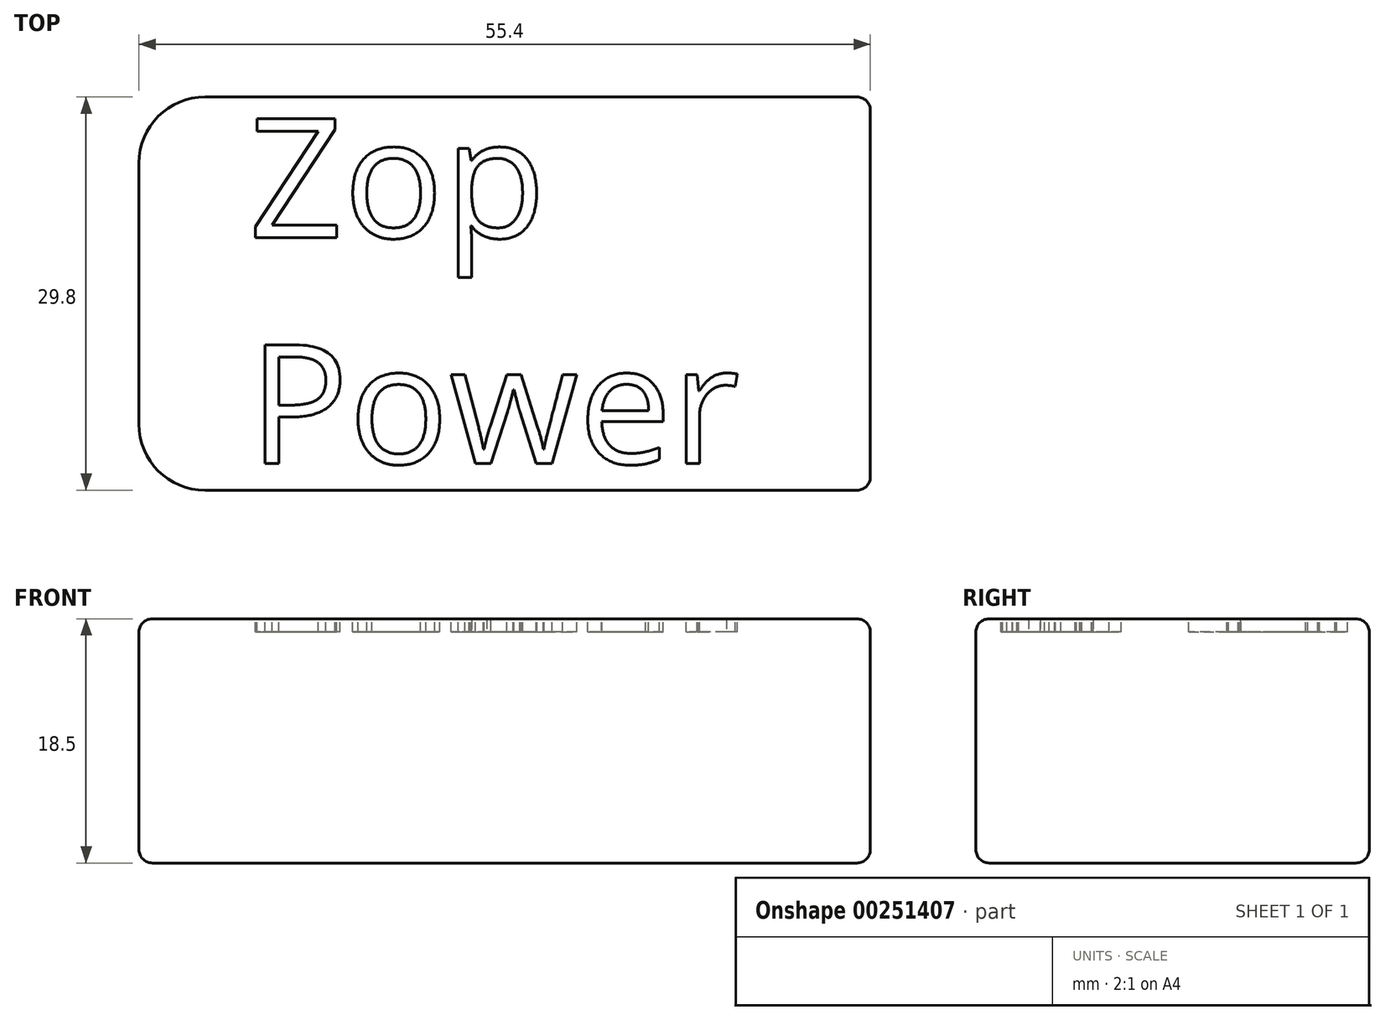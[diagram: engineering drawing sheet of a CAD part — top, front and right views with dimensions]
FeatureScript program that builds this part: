
annotation { "Feature Type Name" : "Feature", "Feature Type Description" : "" }
export const myFeature = defineFeature(function(context is Context, id is Id, definition is map)
    precondition{}
    {
        {
            var Q0;
            Q0=qCreatedBy(makeId("Top.planeOp"),FACE);
            var sketch = newSketch(context, id + "F0", { "sketchPlane" : qUnion([Q0])});
            skLineSegment(sketch, "E0.bottom", {"start": v(27.7, 14.9) * mm, "end": v(-27.7, 14.9) * mm});
            skLineSegment(sketch, "E0.top", {"start": v(27.7, -14.9) * mm, "end": v(-27.7, -14.9) * mm});
            skLineSegment(sketch, "E0.left", {"start": v(27.7, 14.9) * mm, "end": v(27.7, -14.9) * mm});
            skLineSegment(sketch, "E0.right", {"start": v(-27.7, 14.9) * mm, "end": v(-27.7, -14.9) * mm});
            skPoint(sketch, "E0.middle", {"position": v(0, 0) * mm});
            skSolve(sketch);
        }
        {
            var Q0;
            Q0=makeQuery(id+"F0.imprint","IMPRINT",FACE,{"disambiguationData":[TD([[makeQuery(id+"F0.imprint","IMPRINT",EDGE,{"derivedFrom":sQuery(id+"F0.wireOp",EDGE,"E0.bottom")}),1.0]])]});
            extrude(context, id + "F1", {"entities" : qUnion([Q0]), "depth" : 18.5 * mm, "symmetric" : true});
        }
        {
            var Q0;
            Q0=makeQuery(id+"F1.opExtrude","SWEPT_EDGE",EDGE,{"disambiguationData":[OSD([sQuery(id+"F0.wireOp",EDGE,"E0.bottom"),sQuery(id+"F0.wireOp",EDGE,"E0.right")])]});
            var Q1;
            Q1=makeQuery(id+"F1.opExtrude","SWEPT_EDGE",EDGE,{"disambiguationData":[OSD([sQuery(id+"F0.wireOp",EDGE,"E0.top"),sQuery(id+"F0.wireOp",EDGE,"E0.right")])]});
            fillet(context, id + "F2", {"entities" : qUnion([Q0, Q1]), "radius" : 5 * mm, "tangentPropagation" : true, "allowEdgeOverflow" : false});
        }
        {
            var Q0;
            Q0=makeQuery(id+"F1.opExtrude","CAP_FACE",FACE,{"disambiguationData":[OSD([sQuery(id+"F0.wireOp",EDGE,"E0.bottom"),sQuery(id+"F0.wireOp",EDGE,"E0.top"),sQuery(id+"F0.wireOp",EDGE,"E0.left"),sQuery(id+"F0.wireOp",EDGE,"E0.right")])],"isStart":false});
            var Q1;
            Q1=makeQuery(id+"F1.opExtrude","CAP_FACE",FACE,{"disambiguationData":[OSD([sQuery(id+"F0.wireOp",EDGE,"E0.bottom"),sQuery(id+"F0.wireOp",EDGE,"E0.top"),sQuery(id+"F0.wireOp",EDGE,"E0.left"),sQuery(id+"F0.wireOp",EDGE,"E0.right")])],"isStart":true});
            var Q2;
            Q2=makeQuery(id+"F1.opExtrude","SWEPT_FACE",FACE,{"disambiguationData":[OSD([sQuery(id+"F0.wireOp",EDGE,"E0.left")])]});
            fillet(context, id + "F3", {"entities" : qUnion([Q0, Q1, Q2]), "radius" : 1 * mm, "tangentPropagation" : true, "allowEdgeOverflow" : false});
        }
        {
            var Q0;
            Q0=makeQuery(id+"F1.opExtrude","CAP_FACE",FACE,{"disambiguationData":[OSD([sQuery(id+"F0.wireOp",EDGE,"E0.bottom"),sQuery(id+"F0.wireOp",EDGE,"E0.top"),sQuery(id+"F0.wireOp",EDGE,"E0.left"),sQuery(id+"F0.wireOp",EDGE,"E0.right")])],"isStart":false});
            var sketch = newSketch(context, id + "F4", { "sketchPlane" : qUnion([Q0])});
            skText(sketch, "E1", { "text": "Zop\nPower", "fontName": "OpenSans-Regular.ttf"});
            const initialGuessF4  = {"E1": [-0.0194, 0.00425, 1, 0, 0.00907]};
            skSetInitialGuess(sketch, initialGuessF4);
            skSolve(sketch);
        }
        {
            var Q0;
            Q0 = qSketchRegion(id + "F4", true);
            extrude(context, id + "F5", {"entities" : qUnion([Q0]), "operationType" : NewBodyOperationType.REMOVE, "oppositeDirection" : true, "depth" : 1 * mm});
        }
    });
